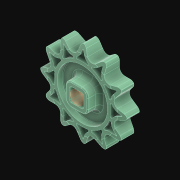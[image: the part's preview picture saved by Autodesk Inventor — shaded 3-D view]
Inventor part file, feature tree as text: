
AUTODESK INVENTOR PART (.ipt)
format: ipt  version: 2021 (Build 250183000, 183)  size: 1,547,264 bytes
history: native  units: in
note: dims shown in document units (in); Inventor stores cm internally (conversion verified against a paired STEP export)
features: other x2, sketch x1, extrude x1
ambient origin geometry x8: Origin, YZ Plane, XZ Plane, XY Plane, X Axis, Y Axis, Z Axis, Center Point
bodies: Solid1 (feature_tree)
feature tree (4):
  sketch  "Sketch1"  dims[d0=0.3937in d1=0.0in]
  other  "Srf1"
  other  "Cut-Extrude3"
  extrude  "ExtrusionSrf1"  [1 undecoded]
note: 1 required parameter value undecoded (feature->parameter linkage not recoverable at this tier; creation-order binding heuristic only, values carry confidence <= 0.55)
